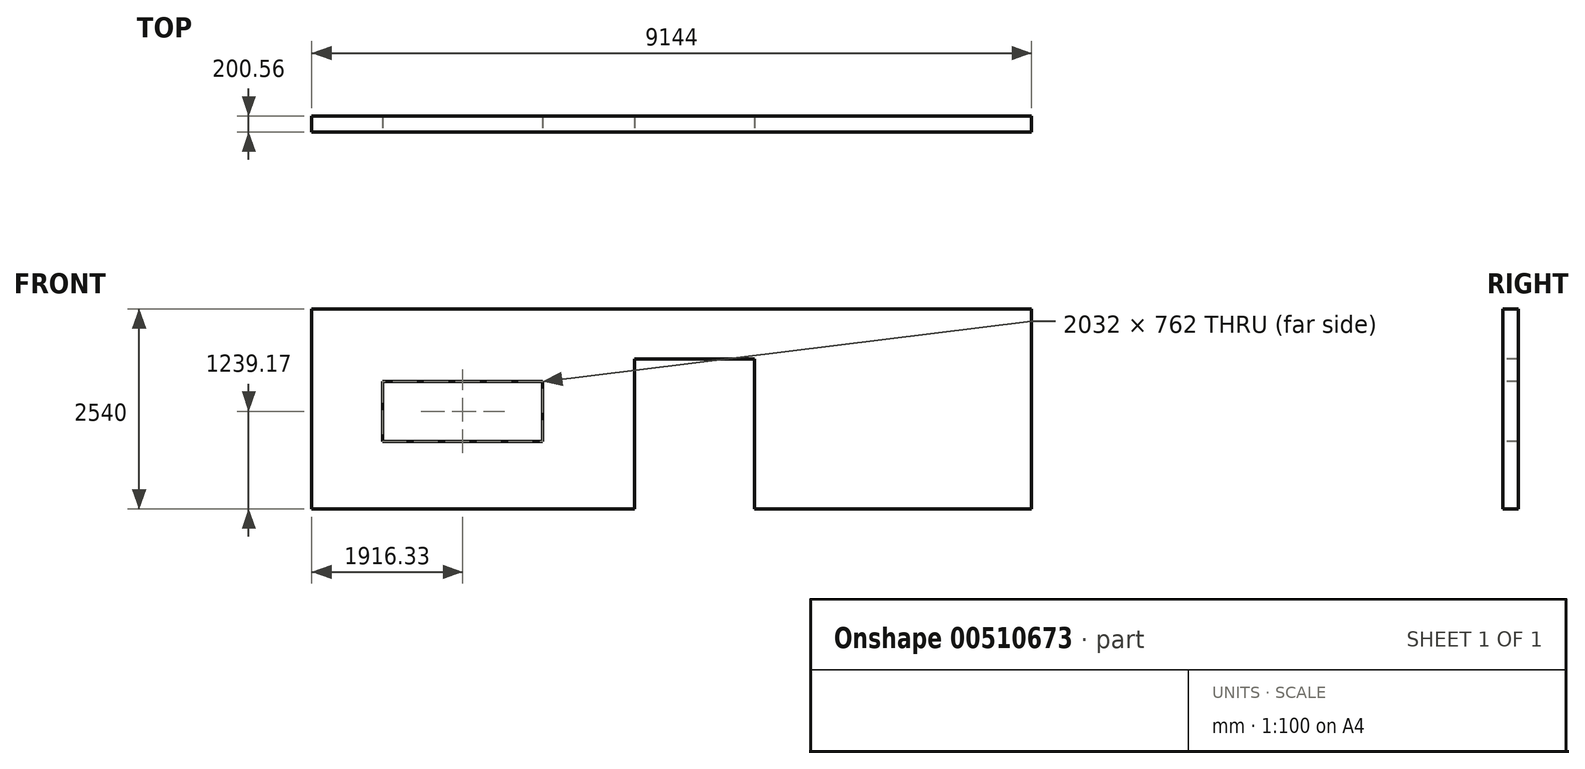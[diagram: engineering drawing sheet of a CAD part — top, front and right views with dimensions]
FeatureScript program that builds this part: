
annotation { "Feature Type Name" : "Feature", "Feature Type Description" : "" }
export const myFeature = defineFeature(function(context is Context, id is Id, definition is map)
    precondition{}
    {
        {
            var Q0;
            Q0=qCreatedBy(makeId("Front.planeOp"),FACE);
            var sketch = newSketch(context, id + "F0", { "sketchPlane" : qUnion([Q0])});
            skLineSegment(sketch, "E0.bottom", {"start": v(-9144, 2540) * mm, "end": v(0, 2540) * mm});
            skLineSegment(sketch, "E0.top", {"start": v(-9144, 0) * mm, "end": v(0, 0) * mm});
            skLineSegment(sketch, "E0.left", {"start": v(-9144, 2540) * mm, "end": v(-9144, 0) * mm});
            skLineSegment(sketch, "E0.right", {"start": v(0, 2540) * mm, "end": v(0, 0) * mm});
            skSolve(sketch);
        }
        {
            var Q0;
            Q0=makeQuery(id+"F0.imprint","IMPRINT",FACE,{"disambiguationData":[TD([[makeQuery(id+"F0.imprint","IMPRINT",EDGE,{"derivedFrom":sQuery(id+"F0.wireOp",EDGE,"E0.bottom")}),-1.0]])]});
            extrude(context, id + "F1", {"entities" : qUnion([Q0]), "depth" : 200.56 * mm, "offsetDistance" : 30.48 * mm});
        }
        {
            var Q0;
            Q0=makeQuery(id+"F1.opExtrude","CAP_FACE",FACE,{"disambiguationData":[OSD([sQuery(id+"F0.wireOp",EDGE,"E0.bottom"),sQuery(id+"F0.wireOp",EDGE,"E0.top"),sQuery(id+"F0.wireOp",EDGE,"E0.left"),sQuery(id+"F0.wireOp",EDGE,"E0.right")])],"isStart":false});
            var sketch = newSketch(context, id + "F2", { "sketchPlane" : qUnion([Q0])});
            skLineSegment(sketch, "E1.bottom", {"start": v(-8243.67, 858.17) * mm, "end": v(-6211.67, 858.17) * mm});
            skLineSegment(sketch, "E1.top", {"start": v(-8243.67, 1620.17) * mm, "end": v(-6211.67, 1620.17) * mm});
            skLineSegment(sketch, "E1.left", {"start": v(-8243.67, 858.17) * mm, "end": v(-8243.67, 1620.17) * mm});
            skLineSegment(sketch, "E1.right", {"start": v(-6211.67, 858.17) * mm, "end": v(-6211.67, 1620.17) * mm});
            skLineSegment(sketch, "E2.bottom", {"start": v(-5042.1, 0) * mm, "end": v(-3518.1, 0) * mm});
            skLineSegment(sketch, "E2.top", {"start": v(-5042.1, 1905) * mm, "end": v(-3518.1, 1905) * mm});
            skLineSegment(sketch, "E2.left", {"start": v(-5042.1, 0) * mm, "end": v(-5042.1, 1905) * mm});
            skLineSegment(sketch, "E2.right", {"start": v(-3518.1, 0) * mm, "end": v(-3518.1, 1905) * mm});
            skSolve(sketch);
        }
        {
            var Q0;
            Q0=makeQuery(id+"F2.imprint","IMPRINT",FACE,{"disambiguationData":[TD([[makeQuery(id+"F2.imprint","IMPRINT",EDGE,{"derivedFrom":sQuery(id+"F2.wireOp",EDGE,"E1.bottom")}),1.0]])]});
            var Q1;
            Q1=makeQuery(id+"F2.imprint","IMPRINT",FACE,{"disambiguationData":[TD([[makeQuery(id+"F2.imprint","IMPRINT",EDGE,{"derivedFrom":sQuery(id+"F2.wireOp",EDGE,"E2.bottom")}),1.0]])]});
            extrude(context, id + "F3", {"entities" : qUnion([Q0, Q1]), "operationType" : NewBodyOperationType.REMOVE, "oppositeDirection" : true, "depth" : 210.3 * mm, "offsetDistance" : 30.48 * mm});
        }
    });
